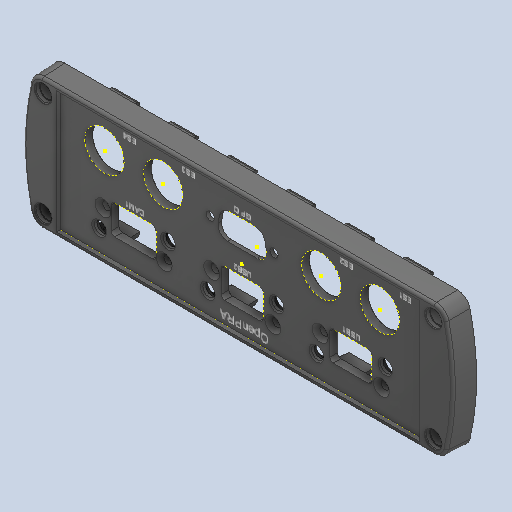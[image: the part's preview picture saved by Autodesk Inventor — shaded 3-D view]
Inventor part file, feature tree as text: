
AUTODESK INVENTOR PART (.ipt)
format: ipt  version: 2024.2 (Build 282272000, 272)  size: 1,131,008 bytes
history: native  units: mm
features: extrude x9, chamfer x4, fillet x3, plane x2, sketch x2, mirror x1, hole x1, projected_geometry x1, other x1
ambient origin geometry x8: Origin, YZ Plane, XZ Plane, XY Plane, X Axis, Y Axis, Z Axis, Center Point
bodies: Solid1 (feature_tree)
feature tree (24):
  extrude  "Extrusion1"  TaperAngle=0.0deg  [1 undecoded]
  fillet  "Fillet1"  Radius=6.9mm
  plane  "Work Plane1"
  extrude  "Extrusion4"  [1 undecoded]
  chamfer  "Chamfer2"  Distance=15.4mm
  mirror  "Mirror1"
  plane  "Work Plane2"
  extrude  "Extrusion6"  Depth=1.0mm
  extrude  "Extrusion7"  Depth=1.0mm
  chamfer  "Chamfer3"  Distance=15.4mm
  extrude  "Extrusion9"  TaperAngle=0.0deg  [1 undecoded]
  fillet  "Fillet3"  Radius=31.0mm
  hole  "Hole1"  [1 undecoded]
  extrude  "Extrusion10"  Depth=0.2mm TaperAngle=45.0deg
  extrude  "Extrusion11"  Depth=1.0mm
  extrude  "Extrusion12"  Depth=1.0mm
  fillet  "Fillet4"  Radius=3.3mm
  chamfer  "Chamfer4"  Distance=12.495mm
  chamfer  "Chamfer5"  Distance=5.23mm
  extrude  "Extrusion13"  Depth=1.0mm
  sketch  "Sketch20"  dims[d23=1.35mm d26=-1.5mm d40=15.4mm d41=11.5mm d42=54.0mm d43=15.4mm d44=0.0mm d45=31.0mm d46=0.0mm d47=0.0mm d48=0.2mm d49=2.0mm d50=45.0deg d53=1.745329mm d54=10.46mm d56=3.3mm d57=12.495mm d58=5.23mm d59=4.77mm d60=0.0mm d61=0.0mm d63=3.72mm d64=9.51mm d65=4.85mm d66=4.85mm d67=27.0mm d68=9.0mm d69=3.3mm d70=3.3mm d71=24.0mm d72=16.55mm d73=11.55mm d74=6.35mm d75=1.85mm d76=5.225mm d77=6.9mm d78=10.075mm d79=10.075mm d80=42.584mm d82=7.0mm d83=10.0mm d84=0.0mm d85=0.5mm d86=2.0mm d87=45.0deg d101=10.075mm d102=4.85mm d103=4.85mm d104=27.0mm d105=9.0mm d106=3.3mm d107=3.3mm d108=24.0mm d109=17.55mm d110=11.55mm d111=6.35mm d112=1.85mm d113=4.725mm d114=10.075mm d115=12.0mm d116=6.9mm d117=42.584mm d118=7.0mm d119=7.0mm d122=12.0mm d123=41.0mm d124=2.0mm d125=0.0mm d126=2.0mm d127=3.25mm d128=6.0mm d129=6.25mm d130=2.0mm d131=90.0deg d132=8.0mm d133=20.594885mm d134=10.0mm d135=0.0mm d136=10.0mm d137=0.0mm d138=0.2mm d139=0.0mm d140=3.0mm d141=0.2mm d142=2.0mm d143=45.0deg d144=0.2mm d145=2.0mm d146=45.0deg d147=10.0mm d148=0.0mm d149=8.0mm d150=12.5mm d151=8.0mm d152=12.5mm d153=12.5mm d154=8.0mm d155=8.0mm d156=12.5mm d157=4.5mm d160=4.5mm d161=1.0mm d164=1.0mm d165=1.0mm d166=2.25mm d167=28.699852mm d169=20.0mm d171=42.584mm d172=10.0mm d174=10.0mm d176=7.0mm d177=7.0mm d178=7.0mm d179=1.0mm d180=4.5mm d181=4.725mm]
  sketch  "Sketch14"  dims[d3=9.0mm d15=0.0mm d16=0.0mm d21=6.9mm]
  projected_geometry  "Projected Loop5"
  other  "1009799_3D"
note: 4 required parameter values undecoded (feature->parameter linkage not recoverable at this tier; creation-order binding heuristic only, values carry confidence <= 0.55)
